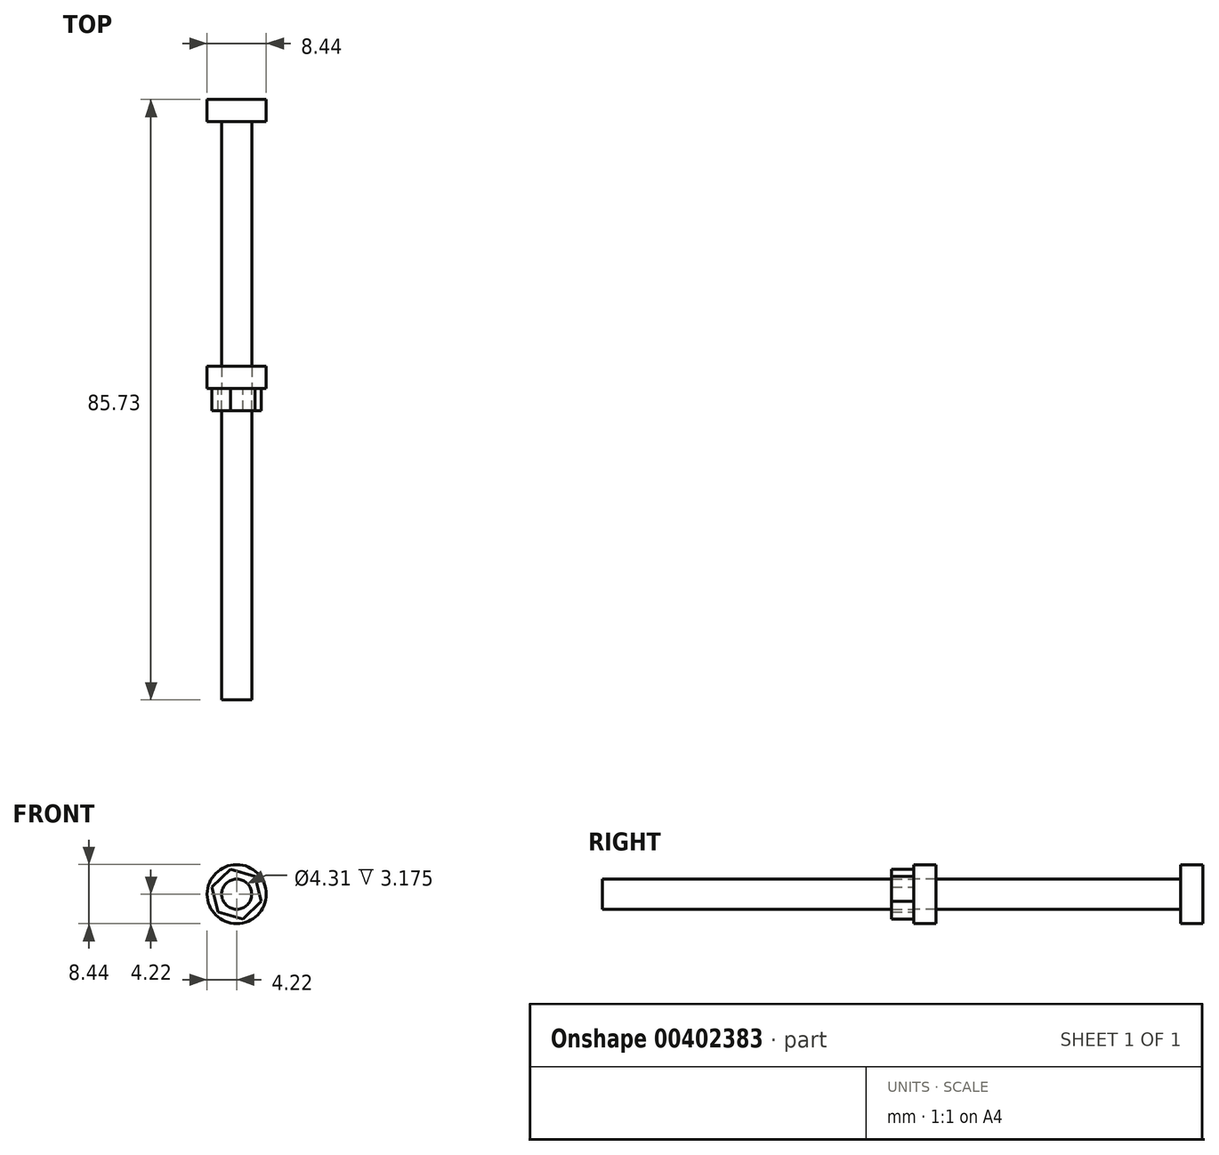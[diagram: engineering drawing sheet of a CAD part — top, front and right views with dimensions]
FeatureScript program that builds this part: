
annotation { "Feature Type Name" : "Feature", "Feature Type Description" : "" }
export const myFeature = defineFeature(function(context is Context, id is Id, definition is map)
    precondition{}
    {
        {
            var Q0;
            Q0=qCreatedBy(makeId("Front.planeOp"),FACE);
            var sketch = newSketch(context, id + "F0", { "sketchPlane" : qUnion([Q0])});
            skCircle(sketch, "E0", {"center": v(0, 0) * mm, "radius": 2.15 * mm});
            skSolve(sketch);
        }
        {
            var Q0;
            Q0 = qSketchRegion(id + "F0", true);
            extrude(context, id + "F1", {"entities" : qUnion([Q0]), "depth" : 44.45 * mm});
        }
        {
            var Q0;
            Q0=makeQuery(id+"F1.opExtrude","CAP_FACE",FACE,{"disambiguationData":[OSD([sQuery(id+"F0.wireOp",EDGE,"E0")])],"isStart":true});
            var sketch = newSketch(context, id + "F2", { "sketchPlane" : qUnion([Q0])});
            skCircle(sketch, "E1", {"center": v(0, 0) * mm, "radius": 4.22 * mm});
            skSolve(sketch);
        }
        {
            var Q0;
            Q0 = qSketchRegion(id + "F2", true);
            extrude(context, id + "F3", {"entities" : qUnion([Q0]), "operationType" : NewBodyOperationType.ADD, "depth" : 3.17 * mm});
        }
        {
            var Q0;
            Q0=qCreatedBy(makeId("Front.planeOp"),FACE);
            var sketch = newSketch(context, id + "F4", { "sketchPlane" : qUnion([Q0])});
            skCircle(sketch, "E2", {"center": v(0, 0) * mm, "radius": 2.15 * mm});
            skCircle(sketch, "E3.cCircle", {"center": v(0, 0) * mm, "radius": 3.18 * mm, "construction": true});
            skLineSegment(sketch, "E3.0", {"start": v(3.53, -1) * mm, "end": v(0.9, -3.56) * mm});
            skLineSegment(sketch, "E3.1", {"start": v(0.9, -3.56) * mm, "end": v(-2.63, -2.55) * mm});
            skLineSegment(sketch, "E3.2", {"start": v(-2.63, -2.55) * mm, "end": v(-3.53, 1) * mm});
            skLineSegment(sketch, "E3.3", {"start": v(-3.53, 1) * mm, "end": v(-0.9, 3.56) * mm});
            skLineSegment(sketch, "E3.4", {"start": v(-0.9, 3.56) * mm, "end": v(2.63, 2.55) * mm});
            skLineSegment(sketch, "E3.5", {"start": v(2.63, 2.55) * mm, "end": v(3.53, -1) * mm});
            skPoint(sketch, "E3.0.midPoint", {"position": v(2.2, -2.28) * mm});
            skSolve(sketch);
        }
        {
            var Q0;
            Q0=makeQuery(id+"F4.imprint","IMPRINT",FACE,{"disambiguationData":[TD([[makeQuery(id+"F4.imprint","IMPRINT",EDGE,{"derivedFrom":sQuery(id+"F4.wireOp",EDGE,"E2")}),-1.0]])]});
            extrude(context, id + "F5", {"entities" : qUnion([Q0]), "depth" : 3.17 * mm});
        }
        {
            var Q0;
            Q0=qCreatedBy(makeId("Front.planeOp"),FACE);
            var sketch = newSketch(context, id + "F6", { "sketchPlane" : qUnion([Q0])});
            skCircle(sketch, "E4", {"center": v(0, 0) * mm, "radius": 2.15 * mm});
            skSolve(sketch);
        }
        {
            var Q0;
            Q0 = qSketchRegion(id + "F6", true);
            extrude(context, id + "F7", {"entities" : qUnion([Q0]), "oppositeDirection" : true, "depth" : 38.1 * mm});
        }
        {
            var Q0;
            Q0=makeQuery(id+"F7.opExtrude","CAP_FACE",FACE,{"disambiguationData":[OSD([sQuery(id+"F6.wireOp",EDGE,"E4")])],"isStart":false});
            var sketch = newSketch(context, id + "F8", { "sketchPlane" : qUnion([Q0])});
            skCircle(sketch, "E5", {"center": v(0, 0) * mm, "radius": 4.22 * mm});
            skSolve(sketch);
        }
        {
            var Q0;
            Q0 = qSketchRegion(id + "F8", true);
            extrude(context, id + "F9", {"entities" : qUnion([Q0]), "operationType" : NewBodyOperationType.ADD, "depth" : 3.17 * mm});
        }
    });
